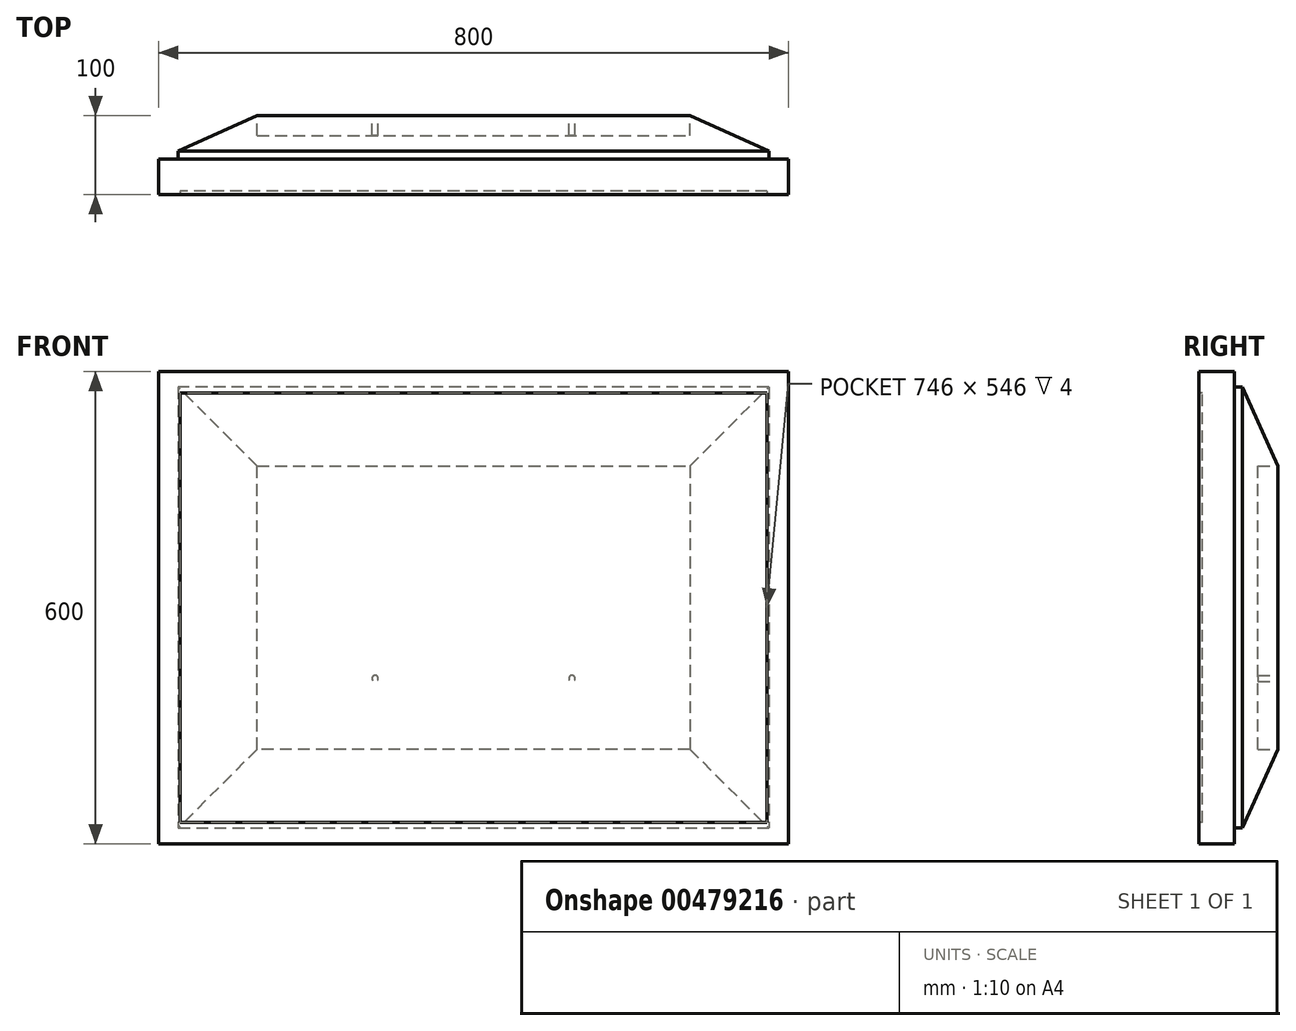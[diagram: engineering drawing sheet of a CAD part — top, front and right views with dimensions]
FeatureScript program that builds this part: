
annotation { "Feature Type Name" : "Feature", "Feature Type Description" : "" }
export const myFeature = defineFeature(function(context is Context, id is Id, definition is map)
    precondition{}
    {
        {
            var Q0;
            Q0=qCreatedBy(makeId("Right.planeOp"),FACE);
            var sketch = newSketch(context, id + "F0", { "sketchPlane" : qUnion([Q0])});
            skLineSegment(sketch, "E0.bottom", {"start": v(-22.5, 300) * mm, "end": v(22.5, 300) * mm});
            skLineSegment(sketch, "E0.top", {"start": v(-22.5, -300) * mm, "end": v(22.5, -300) * mm});
            skLineSegment(sketch, "E0.left", {"start": v(-22.5, 300) * mm, "end": v(-22.5, -300) * mm});
            skLineSegment(sketch, "E0.right", {"start": v(22.5, 300) * mm, "end": v(22.5, -300) * mm});
            skPoint(sketch, "E0.middle", {"position": v(0, 0) * mm});
            skLineSegment(sketch, "E1.bottom", {"start": v(22.5, 280) * mm, "end": v(77.5, 280) * mm});
            skLineSegment(sketch, "E1.top", {"start": v(22.5, -280) * mm, "end": v(77.5, -280) * mm});
            skLineSegment(sketch, "E1.left", {"start": v(22.5, 280) * mm, "end": v(22.5, -280) * mm});
            skLineSegment(sketch, "E1.right", {"start": v(77.5, 280) * mm, "end": v(77.5, -280) * mm});
            skSolve(sketch);
        }
        {
            var Q0;
            {var subQ1=sQuery(id+"F0.wireOp",EDGE,"E0.bottom");Q0=makeQuery(id+"F0.imprint","IMPRINT",FACE,{"disambiguationData":[TD([[makeQuery(id+"F0.imprint","IMPRINT",EDGE,{"derivedFrom":subQ1}),-1.0]])]});}
            var Q1;
            Q1=makeQuery(id+"F0.imprint","IMPRINT",FACE,{"disambiguationData":[TD([[makeQuery(id+"F0.imprint","IMPRINT",EDGE,{"derivedFrom":sQuery(id+"F0.wireOp",EDGE,"E1.bottom")}),-1.0]])]});
            extrude(context, id + "F1", {"entities" : qUnion([Q0, Q1]), "depth" : 800 * mm});
        }
        {
            var Q0;
            Q0=makeQuery(id+"F1.opExtrude","CAP_FACE",FACE,{"disambiguationData":[OSD([sQuery(id+"F0.wireOp",EDGE,"E0.bottom"),sQuery(id+"F0.wireOp",EDGE,"E0.top"),sQuery(id+"F0.wireOp",EDGE,"E0.left"),sQuery(id+"F0.wireOp",EDGE,"E0.right"),sQuery(id+"F0.wireOp",EDGE,"E1.bottom"),sQuery(id+"F0.wireOp",EDGE,"E1.top"),sQuery(id+"F0.wireOp",EDGE,"E1.right")])],"isStart":false});
            var sketch = newSketch(context, id + "F2", { "sketchPlane" : qUnion([Q0])});
            skLineSegment(sketch, "E2.bottom", {"start": v(22.5, 280) * mm, "end": v(77.5, 280) * mm});
            skLineSegment(sketch, "E2.top", {"start": v(22.5, -280) * mm, "end": v(77.5, -280) * mm});
            skLineSegment(sketch, "E2.left", {"start": v(22.5, 280) * mm, "end": v(22.5, -280) * mm});
            skLineSegment(sketch, "E2.right", {"start": v(77.5, 280) * mm, "end": v(77.5, -280) * mm});
            skSolve(sketch);
        }
        {
            var Q0;
            Q0=makeQuery(id+"F2.imprint","IMPRINT",FACE,{"disambiguationData":[TD([[makeQuery(id+"F2.imprint","IMPRINT",EDGE,{"derivedFrom":sQuery(id+"F2.wireOp",EDGE,"E2.bottom")}),-1.0]])]});
            var Q1;
            Q1=makeQuery(id+"F0.imprint","IMPRINT",FACE,{"disambiguationData":[TD([[makeQuery(id+"F0.imprint","IMPRINT",EDGE,{"derivedFrom":sQuery(id+"F0.wireOp",EDGE,"E1.bottom")}),-1.0]])]});
            extrude(context, id + "F3", {"entities" : qUnion([Q0, Q1]), "operationType" : NewBodyOperationType.REMOVE, "oppositeDirection" : true, "depth" : 50 * mm, "symmetric" : true});
        }
        {
            var Q0;
            Q0=makeQuery(id+"F1.opExtrude","SWEPT_FACE",FACE,{"disambiguationData":[OSD([sQuery(id+"F0.wireOp",EDGE,"E1.right")])]});
            chamfer(context, id + "F4", {"entities" : qUnion([Q0]), "chamferType" : ChamferType.TWO_OFFSETS, "width1" : 45 * mm, "oppositeDirection" : false, "width2" : 100 * mm, "tangentPropagation" : true});
        }
        {
            var Q0;
            Q0=makeQuery(id+"F1.opExtrude","SWEPT_FACE",FACE,{"disambiguationData":[OSD([sQuery(id+"F0.wireOp",EDGE,"E0.left")])]});
            var sketch = newSketch(context, id + "F5", { "sketchPlane" : qUnion([Q0])});
            skLineSegment(sketch, "E3.bottom", {"start": v(773, -273) * mm, "end": v(27, -273) * mm});
            skLineSegment(sketch, "E3.top", {"start": v(773, 273) * mm, "end": v(27, 273) * mm});
            skLineSegment(sketch, "E3.left", {"start": v(773, -273) * mm, "end": v(773, 273) * mm});
            skLineSegment(sketch, "E3.right", {"start": v(27, -273) * mm, "end": v(27, 273) * mm});
            skPoint(sketch, "E3.middle", {"position": v(400, 0) * mm});
            skPoint(sketch, "E3.middle.positionSnap0", {"position": v(400, 300) * mm});
            skPoint(sketch, "E3.middle.positionSnap1", {"position": v(0, 0) * mm});
            skPoint(sketch, "E3.centerSnap0", {"position": v(400, 300) * mm});
            skPoint(sketch, "E3.centerSnap1", {"position": v(0, 0) * mm});
            skSolve(sketch);
        }
        {
            var Q0;
            Q0=makeQuery(id+"F5.imprint","IMPRINT",FACE,{"disambiguationData":[TD([[makeQuery(id+"F5.imprint","IMPRINT",EDGE,{"derivedFrom":sQuery(id+"F5.wireOp",EDGE,"E3.bottom")}),-1.0]])]});
            extrude(context, id + "F6", {"entities" : qUnion([Q0]), "operationType" : NewBodyOperationType.REMOVE, "oppositeDirection" : true, "depth" : 4 * mm});
        }
        {
            var Q0;
            Q0=makeQuery(id+"F1.opExtrude","SWEPT_FACE",FACE,{"disambiguationData":[OSD([sQuery(id+"F0.wireOp",EDGE,"E1.right")])]});
            var sketch = newSketch(context, id + "F7", { "sketchPlane" : qUnion([Q0])});
            skLineSegment(sketch, "E4.bottom", {"start": v(-525, -135) * mm, "end": v(-275, -135) * mm});
            skLineSegment(sketch, "E4.top", {"start": v(-525, 135) * mm, "end": v(-275, 135) * mm});
            skLineSegment(sketch, "E4.left", {"start": v(-525, -135) * mm, "end": v(-525, 135) * mm});
            skLineSegment(sketch, "E4.right", {"start": v(-275, -135) * mm, "end": v(-275, 135) * mm});
            skPoint(sketch, "E4.middle", {"position": v(-400, 0) * mm});
            skPoint(sketch, "E4.middle.positionSnap0", {"position": v(-400, 180) * mm});
            skPoint(sketch, "E4.centerSnap0", {"position": v(-400, 180) * mm});
            skCircle(sketch, "E5", {"center": v(-525, 90) * mm, "radius": 4 * mm});
            skCircle(sketch, "E6", {"center": v(-525, -90) * mm, "radius": 4 * mm});
            skCircle(sketch, "E7", {"center": v(-275, -90) * mm, "radius": 4 * mm});
            skCircle(sketch, "E8", {"center": v(-275, 90) * mm, "radius": 4 * mm});
            skSolve(sketch);
        }
        {
            var Q0;
            {var subQ0=sQuery(id+"F7.wireOp",EDGE,"E5");var subQ1=sQuery(id+"F7.wireOp",EDGE,"E4.left");var subQ2=makeQuery(id+"F7.imprint","INTERSECT",VERTEX,{"disambiguationData":[OD(0.0)],"derivedFrom":[subQ1,subQ0]});Q0=makeQuery(id+"F7.imprint","IMPRINT",FACE,{"disambiguationData":[TD([[makeQuery(id+"F7.imprint","IMPRINT",EDGE,{"disambiguationData":[TD([[subQ2,-1.0]])],"derivedFrom":subQ1}),1.0]])]});}
            var Q1;
            {var subQ0=sQuery(id+"F7.wireOp",EDGE,"E5");var subQ1=sQuery(id+"F7.wireOp",EDGE,"E4.left");var subQ2=makeQuery(id+"F7.imprint","INTERSECT",VERTEX,{"disambiguationData":[OD(0.0)],"derivedFrom":[subQ1,subQ0]});Q1=makeQuery(id+"F7.imprint","IMPRINT",FACE,{"disambiguationData":[TD([[makeQuery(id+"F7.imprint","IMPRINT",EDGE,{"disambiguationData":[TD([[subQ2,-1.0]])],"derivedFrom":subQ1}),-1.0]])]});}
            var Q2;
            {var subQ0=sQuery(id+"F7.wireOp",EDGE,"E6");var subQ1=sQuery(id+"F7.wireOp",EDGE,"E4.left");var subQ2=makeQuery(id+"F7.imprint","INTERSECT",VERTEX,{"disambiguationData":[OD(0.0)],"derivedFrom":[subQ1,subQ0]});Q2=makeQuery(id+"F7.imprint","IMPRINT",FACE,{"disambiguationData":[TD([[makeQuery(id+"F7.imprint","IMPRINT",EDGE,{"disambiguationData":[TD([[subQ2,-1.0]])],"derivedFrom":subQ1}),1.0]])]});}
            var Q3;
            {var subQ0=sQuery(id+"F7.wireOp",EDGE,"E6");var subQ1=sQuery(id+"F7.wireOp",EDGE,"E4.left");var subQ2=makeQuery(id+"F7.imprint","INTERSECT",VERTEX,{"disambiguationData":[OD(0.0)],"derivedFrom":[subQ1,subQ0]});Q3=makeQuery(id+"F7.imprint","IMPRINT",FACE,{"disambiguationData":[TD([[makeQuery(id+"F7.imprint","IMPRINT",EDGE,{"disambiguationData":[TD([[subQ2,-1.0]])],"derivedFrom":subQ1}),-1.0]])]});}
            var Q4;
            {var subQ0=sQuery(id+"F7.wireOp",EDGE,"E7");var subQ1=sQuery(id+"F7.wireOp",EDGE,"E4.right");var subQ2=makeQuery(id+"F7.imprint","INTERSECT",VERTEX,{"disambiguationData":[OD(0.0)],"derivedFrom":[subQ1,subQ0]});Q4=makeQuery(id+"F7.imprint","IMPRINT",FACE,{"disambiguationData":[TD([[makeQuery(id+"F7.imprint","IMPRINT",EDGE,{"disambiguationData":[TD([[subQ2,-1.0]])],"derivedFrom":subQ1}),1.0]])]});}
            var Q5;
            {var subQ0=sQuery(id+"F7.wireOp",EDGE,"E7");var subQ1=sQuery(id+"F7.wireOp",EDGE,"E4.right");var subQ2=makeQuery(id+"F7.imprint","INTERSECT",VERTEX,{"disambiguationData":[OD(0.0)],"derivedFrom":[subQ1,subQ0]});Q5=makeQuery(id+"F7.imprint","IMPRINT",FACE,{"disambiguationData":[TD([[makeQuery(id+"F7.imprint","IMPRINT",EDGE,{"disambiguationData":[TD([[subQ2,-1.0]])],"derivedFrom":subQ1}),-1.0]])]});}
            var Q6;
            {var subQ0=sQuery(id+"F7.wireOp",EDGE,"E8");var subQ1=sQuery(id+"F7.wireOp",EDGE,"E4.right");var subQ2=makeQuery(id+"F7.imprint","INTERSECT",VERTEX,{"disambiguationData":[OD(0.0)],"derivedFrom":[subQ1,subQ0]});Q6=makeQuery(id+"F7.imprint","IMPRINT",FACE,{"disambiguationData":[TD([[makeQuery(id+"F7.imprint","IMPRINT",EDGE,{"disambiguationData":[TD([[subQ2,-1.0]])],"derivedFrom":subQ1}),1.0]])]});}
            var Q7;
            {var subQ0=sQuery(id+"F7.wireOp",EDGE,"E8");var subQ1=sQuery(id+"F7.wireOp",EDGE,"E4.right");var subQ2=makeQuery(id+"F7.imprint","INTERSECT",VERTEX,{"disambiguationData":[OD(0.0)],"derivedFrom":[subQ1,subQ0]});Q7=makeQuery(id+"F7.imprint","IMPRINT",FACE,{"disambiguationData":[TD([[makeQuery(id+"F7.imprint","IMPRINT",EDGE,{"disambiguationData":[TD([[subQ2,-1.0]])],"derivedFrom":subQ1}),-1.0]])]});}
            extrude(context, id + "F8", {"entities" : qUnion([Q0, Q1, Q2, Q3, Q4, Q5, Q6, Q7]), "operationType" : NewBodyOperationType.REMOVE, "oppositeDirection" : true, "depth" : 25 * mm});
        }
    });
